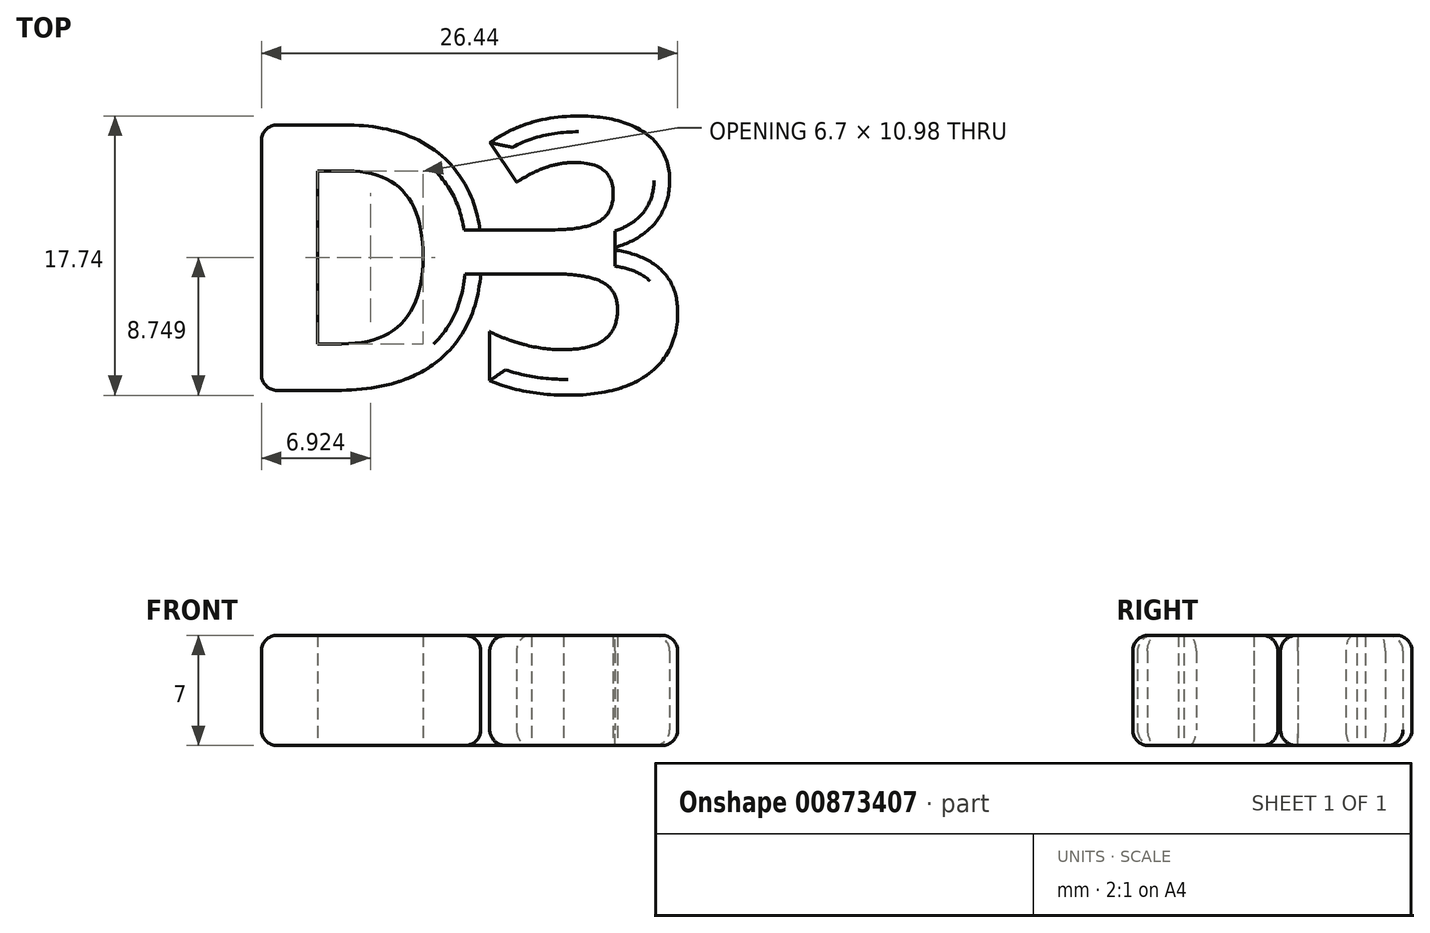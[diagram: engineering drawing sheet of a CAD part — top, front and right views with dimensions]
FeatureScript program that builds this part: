
annotation { "Feature Type Name" : "Feature", "Feature Type Description" : "" }
export const myFeature = defineFeature(function(context is Context, id is Id, definition is map)
    precondition{}
    {
        {
            var Q0;
            Q0=qCreatedBy(makeId("Top.planeOp"),FACE);
            var sketch = newSketch(context, id + "F0", { "sketchPlane" : qUnion([Q0])});
            skText(sketch, "E0", { "text": "D", "fontName": "OpenSans-Bold.ttf"});
            skText(sketch, "E1", { "text": "3", "fontName": "OpenSans-Bold.ttf"});
            skLineSegment(sketch, "E2.bottom", {"start": v(5.57, 1.32) * mm, "end": v(-5.64, 1.32) * mm});
            skLineSegment(sketch, "E2.top", {"start": v(5.57, -1.48) * mm, "end": v(-5.64, -1.48) * mm});
            skLineSegment(sketch, "E2.left", {"start": v(5.57, 1.32) * mm, "end": v(5.57, -1.48) * mm});
            skLineSegment(sketch, "E2.right", {"start": v(-5.64, 1.32) * mm, "end": v(-5.64, -1.48) * mm});
            const initialGuessF0  = {"E0": [-0.019, -0.00886, 1, 0, 0.017], "E1": [-0.0033, -0.00893, 1, 0, 0.0174]};
            skSetInitialGuess(sketch, initialGuessF0);
            skSolve(sketch);
        }
        {
            var Q0;
            Q0 = qSketchRegion(id + "F0", true);
            extrude(context, id + "F1", {"entities" : qUnion([Q0]), "depth" : 7 * mm, "offsetDistance" : 25 * mm});
        }
        {
            var Q0;
            Q0=makeQuery(id+"F1.opExtrude","CAP_EDGE",EDGE,{"disambiguationData":[OSD([sQuery(id+"F0.wireOp",EDGE,"E0.sketch_text.stroke-3")])],"isStart":false});
            var Q1;
            Q1=makeQuery(id+"F1.opExtrude","SWEPT_EDGE",EDGE,{"disambiguationData":[OSD([sQuery(id+"F0.wireOp",EDGE,"E0.sketch_text.stroke-2"),sQuery(id+"F0.wireOp",EDGE,"E0.sketch_text.stroke-3")])]});
            var Q2;
            Q2=makeQuery(id+"F1.opExtrude","CAP_EDGE",EDGE,{"disambiguationData":[OSD([sQuery(id+"F0.wireOp",EDGE,"E0.sketch_text.stroke-2")])],"isStart":true});
            var Q3;
            Q3=makeQuery(id+"F1.opExtrude","CAP_EDGE",EDGE,{"disambiguationData":[OSD([sQuery(id+"F0.wireOp",EDGE,"E0.sketch_text.stroke-3")])],"isStart":true});
            var Q4;
            Q4=makeQuery(id+"F1.opExtrude","SWEPT_EDGE",EDGE,{"disambiguationData":[OSD([sQuery(id+"F0.wireOp",EDGE,"E0.sketch_text.stroke-3"),sQuery(id+"F0.wireOp",EDGE,"E0.sketch_text.stroke-4")])]});
            var Q5;
            Q5=makeQuery(id+"F1.opExtrude","CAP_EDGE",EDGE,{"disambiguationData":[OSD([sQuery(id+"F0.wireOp",EDGE,"E0.sketch_text.stroke-4")])],"isStart":false});
            var Q6;
            Q6=makeQuery(id+"F1.opExtrude","CAP_EDGE",EDGE,{"disambiguationData":[OSD([sQuery(id+"F0.wireOp",EDGE,"E0.sketch_text.stroke-5")])],"isStart":false});
            var Q7;
            Q7=makeQuery(id+"F1.opExtrude","CAP_EDGE",EDGE,{"disambiguationData":[OSD([sQuery(id+"F0.wireOp",EDGE,"E0.sketch_text.stroke-6")])],"isStart":false});
            var Q8;
            Q8=makeQuery(id+"F1.opExtrude","CAP_EDGE",EDGE,{"disambiguationData":[OSD([sQuery(id+"F0.wireOp",EDGE,"E0.sketch_text.stroke-1")])],"isStart":false});
            var Q9;
            Q9=makeQuery(id+"F1.opExtrude","CAP_EDGE",EDGE,{"disambiguationData":[OSD([sQuery(id+"F0.wireOp",EDGE,"E0.sketch_text.stroke-0")])],"isStart":false});
            var Q10;
            Q10=makeQuery(id+"F1.opExtrude","CAP_EDGE",EDGE,{"disambiguationData":[OSD([sQuery(id+"F0.wireOp",EDGE,"E1.sketch_text.stroke-6")])],"isStart":false});
            var Q11;
            Q11=makeQuery(id+"F1.opExtrude","CAP_EDGE",EDGE,{"disambiguationData":[OSD([sQuery(id+"F0.wireOp",EDGE,"E1.sketch_text.stroke-4")])],"isStart":false});
            var Q12;
            Q12=makeQuery(id+"F1.opExtrude","CAP_EDGE",EDGE,{"disambiguationData":[OSD([sQuery(id+"F0.wireOp",EDGE,"E1.sketch_text.stroke-1")])],"isStart":false});
            var Q13;
            Q13=makeQuery(id+"F1.opExtrude","CAP_EDGE",EDGE,{"disambiguationData":[OSD([sQuery(id+"F0.wireOp",EDGE,"E1.sketch_text.stroke-26")])],"isStart":false});
            var Q14;
            Q14=makeQuery(id+"F1.opExtrude","CAP_EDGE",EDGE,{"disambiguationData":[OSD([sQuery(id+"F0.wireOp",EDGE,"E1.sketch_text.stroke-24")])],"isStart":false});
            var Q15;
            Q15=makeQuery(id+"F1.opExtrude","CAP_EDGE",EDGE,{"disambiguationData":[OSD([sQuery(id+"F0.wireOp",EDGE,"E1.sketch_text.stroke-25")])],"isStart":false});
            var Q16;
            Q16=makeQuery(id+"F1.opExtrude","CAP_EDGE",EDGE,{"disambiguationData":[OSD([sQuery(id+"F0.wireOp",EDGE,"E1.sketch_text.stroke-7")])],"isStart":false});
            var Q17;
            Q17=makeQuery(id+"F1.opExtrude","CAP_EDGE",EDGE,{"disambiguationData":[OSD([sQuery(id+"F0.wireOp",EDGE,"E1.sketch_text.stroke-8")])],"isStart":false});
            var Q18;
            Q18=makeQuery(id+"F1.opExtrude","CAP_EDGE",EDGE,{"disambiguationData":[OSD([sQuery(id+"F0.wireOp",EDGE,"E1.sketch_text.stroke-23")])],"isStart":false});
            var Q19;
            Q19=makeQuery(id+"F1.opExtrude","CAP_EDGE",EDGE,{"disambiguationData":[OSD([sQuery(id+"F0.wireOp",EDGE,"E1.sketch_text.stroke-5")])],"isStart":true});
            var Q20;
            Q20=makeQuery(id+"F1.opExtrude","CAP_EDGE",EDGE,{"disambiguationData":[OSD([sQuery(id+"F0.wireOp",EDGE,"E1.sketch_text.stroke-0")])],"isStart":true});
            var Q21;
            Q21=makeQuery(id+"F1.opExtrude","CAP_EDGE",EDGE,{"disambiguationData":[OSD([sQuery(id+"F0.wireOp",EDGE,"E1.sketch_text.stroke-23")])],"isStart":true});
            var Q22;
            Q22=makeQuery(id+"F1.opExtrude","CAP_EDGE",EDGE,{"disambiguationData":[OSD([sQuery(id+"F0.wireOp",EDGE,"E1.sketch_text.stroke-8")])],"isStart":true});
            var Q23;
            Q23=makeQuery(id+"F1.opExtrude","CAP_EDGE",EDGE,{"disambiguationData":[OSD([sQuery(id+"F0.wireOp",EDGE,"E0.sketch_text.stroke-6")])],"isStart":true});
            fillet(context, id + "F2", {"entities" : qUnion([Q0, Q1, Q2, Q3, Q4, Q5, Q6, Q7, Q8, Q9, Q10, Q11, Q12, Q13, Q14, Q15, Q16, Q17, Q18, Q19, Q20, Q21, Q22, Q23]), "radius" : 1 * mm, "tangentPropagation" : true, "allowEdgeOverflow" : false});
        }
    });
